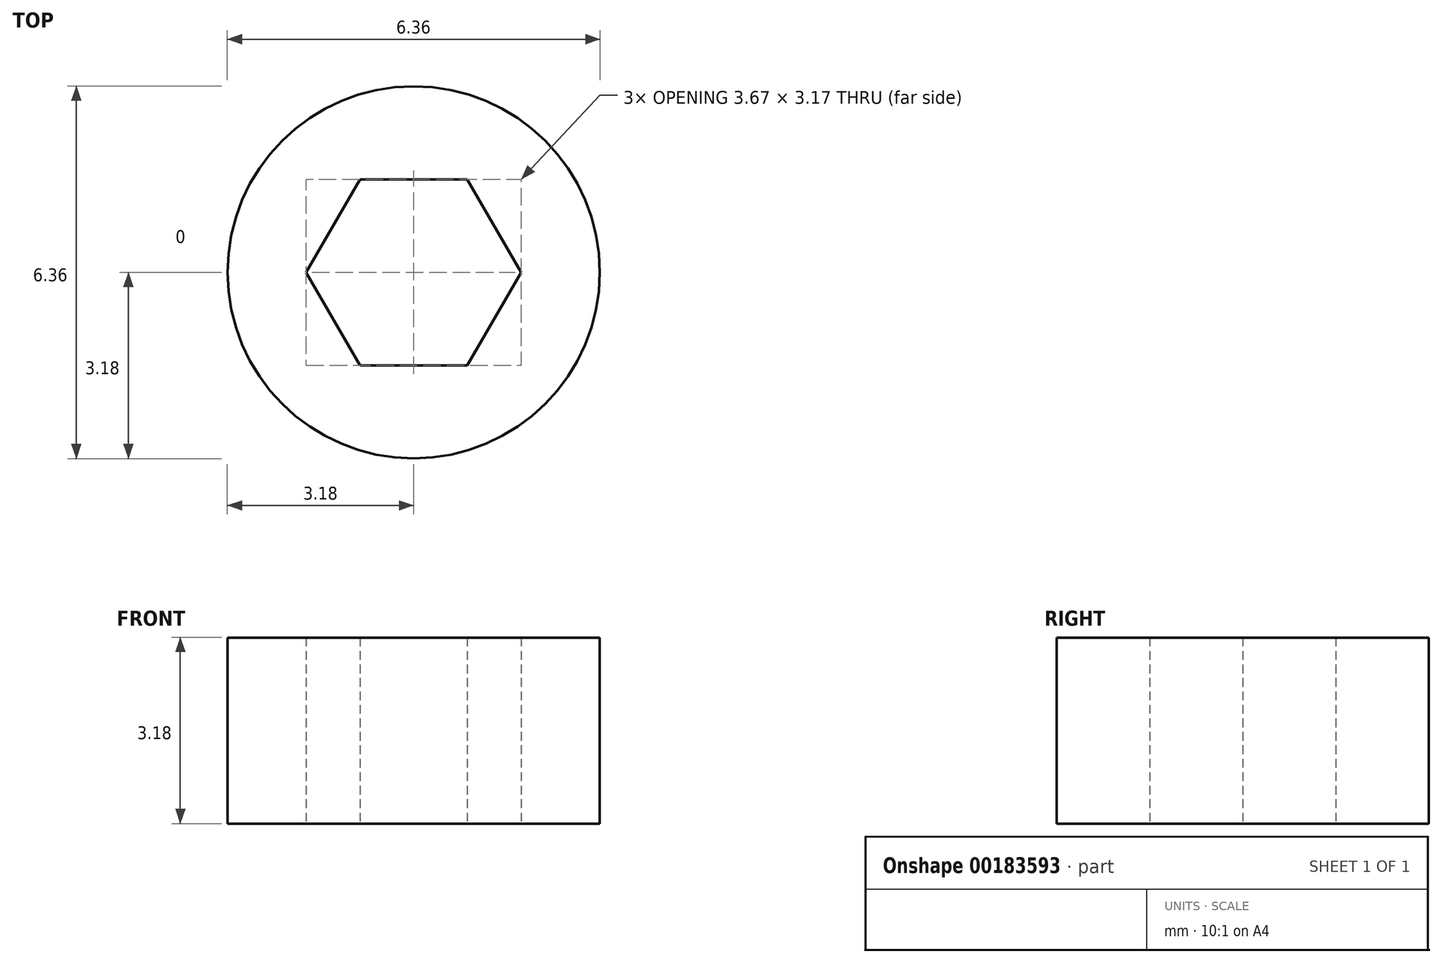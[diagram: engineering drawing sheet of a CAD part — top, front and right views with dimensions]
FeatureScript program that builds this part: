
annotation { "Feature Type Name" : "Feature", "Feature Type Description" : "" }
export const myFeature = defineFeature(function(context is Context, id is Id, definition is map)
    precondition{}
    {
        {
            var Q0;
            Q0=qCreatedBy(makeId("Top.planeOp"),FACE);
            var sketch = newSketch(context, id + "F0", { "sketchPlane" : qUnion([Q0])});
            skCircle(sketch, "E0", {"center": v(0, 0) * mm, "radius": 3.18 * mm});
            skCircle(sketch, "E1.cCircle", {"center": v(0, 0) * mm, "radius": 1.59 * mm, "construction": true});
            skLineSegment(sketch, "E1.0", {"start": v(-0.92, 1.59) * mm, "end": v(0.92, 1.59) * mm});
            skLineSegment(sketch, "E1.1", {"start": v(0.92, 1.59) * mm, "end": v(1.83, 0) * mm});
            skLineSegment(sketch, "E1.2", {"start": v(1.83, 0) * mm, "end": v(0.92, -1.59) * mm});
            skLineSegment(sketch, "E1.3", {"start": v(0.92, -1.59) * mm, "end": v(-0.92, -1.59) * mm});
            skLineSegment(sketch, "E1.4", {"start": v(-0.92, -1.59) * mm, "end": v(-1.83, 0) * mm});
            skLineSegment(sketch, "E1.5", {"start": v(-1.83, 0) * mm, "end": v(-0.92, 1.59) * mm});
            skPoint(sketch, "E1.0.midPoint", {"position": v(0, 1.59) * mm});
            skSolve(sketch);
        }
        {
            var Q0;
            Q0 = qSketchRegion(id + "F0", true);
            extrude(context, id + "F1", {"entities" : qUnion([Q0]), "depth" : 3.17 * mm});
        }
        {
            var Q0;
            Q0=qCreatedBy(makeId("Top.planeOp"),FACE);
            var sketch = newSketch(context, id + "F2", { "sketchPlane" : qUnion([Q0])});
            skCircle(sketch, "E2", {"center": v(0, 0) * mm, "radius": 1.59 * mm});
            skSolve(sketch);
        }
        {
            var Q0;
            Q0 = qSketchRegion(id + "F2", true);
            extrude(context, id + "F3", {"entities" : qUnion([Q0]), "operationType" : NewBodyOperationType.REMOVE, "oppositeDirection" : true, "depth" : 34.92 * mm});
        }
    });
